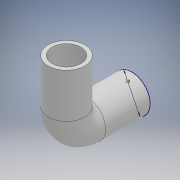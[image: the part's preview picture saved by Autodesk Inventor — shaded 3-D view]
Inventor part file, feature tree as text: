
AUTODESK INVENTOR PART (.ipt)
format: ipt  version: 2017 (Build 210142000, 142)  size: 147,456 bytes
history: native  units: mm
features: sketch x3, plane x2, sweep x1, shell x1
ambient origin geometry x8: Origin, YZ Plane, XZ Plane, XY Plane, X Axis, Y Axis, Z Axis, Center Point
bodies: Solid1 (feature_tree)
feature tree (7):
  plane  "Work Plane1"
  sketch  "Sketch1"  dims[d0=50.0mm d1=28.0mm d2=50.0mm]
  plane  "Work Plane2"
  sketch  "Sketch2"  dims[d3=28.0mm]
  sweep  "Sweep1"
  shell  "Shell1"  Thickness=50.0mm
  sketch  "Sketch3"  dims[d4=2.0mm d5=0.0mm d6=0.0mm d7=3.0mm]
